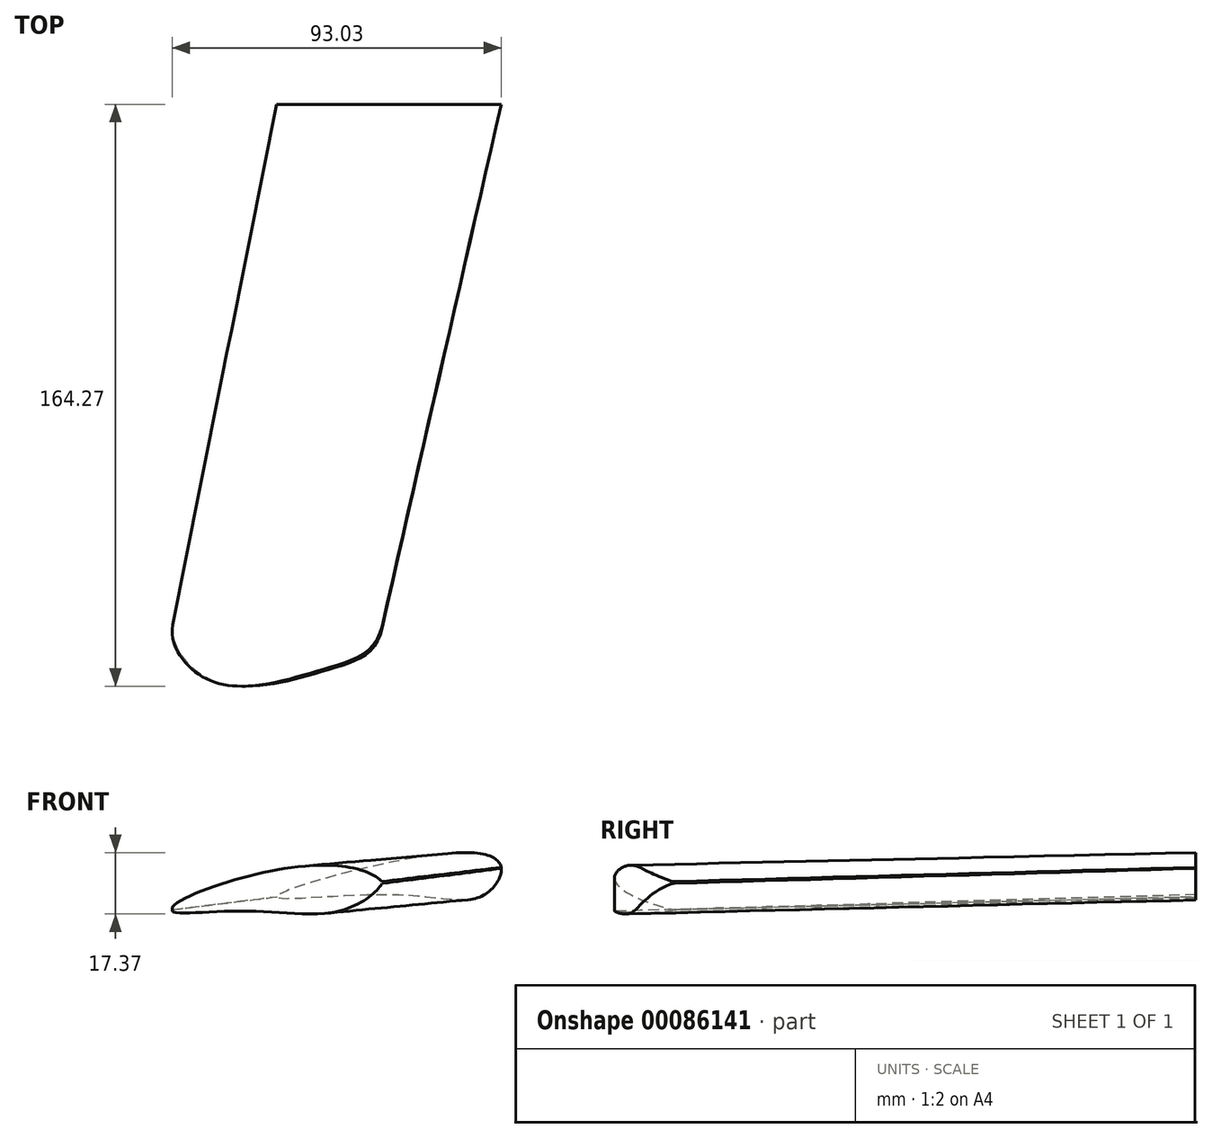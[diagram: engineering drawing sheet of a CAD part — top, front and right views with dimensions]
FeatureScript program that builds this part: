
annotation { "Feature Type Name" : "Feature", "Feature Type Description" : "" }
export const myFeature = defineFeature(function(context is Context, id is Id, definition is map)
    precondition{}
    {
        {
            var Q0;
            Q0=qCreatedBy(makeId("Front.planeOp"),FACE);
            var sketch = newSketch(context, id + "F0", { "sketchPlane" : qUnion([Q0])});
            skPoint(sketch, "E0.4.internal.orphan", {"position": v(0, 8.33) * mm});
            skFitSpline(sketch, "E1", {"points": [v(8.73, 20.08) * mm, v(-3.65, 24.53) * mm, v(-54.77, 12.14) * mm, v(-21.27, 12.62) * mm, v(3.33, 12.3) * mm, v(8.73, 20.08) * mm]});
            skLineSegment(sketch, "E2", {"start": v(8.73, 20.08) * mm, "end": v(-54.77, 12.14) * mm, "construction": true});
            skSolve(sketch);
        }
        {
            var Q0;
            Q0=qCreatedBy(makeId("Front.planeOp"),FACE);
            cPlane(context, id + "F1", {"entities" : qUnion([Q0]), "cplaneType" : CPlaneType.OFFSET, "offset" : 165.1 * mm, "width" : 152.4 * mm, "height" : 152.4 * mm});
        }
        {
            var Q0;
            Q0=sQuery(id+"F0.wireOp",EDGE,"E2");
            cPlane(context, id + "F2", {"entities" : qUnion([Q0]), "cplaneType" : CPlaneType.LINE_ANGLE, "offset" : 152.4 * mm, "angle" : 90 * degree, "width" : 152.4 * mm, "height" : 152.4 * mm});
        }
        {
            var Q0;
            Q0=qCreatedBy(id+"F2.planeOp",FACE);
            var sketch = newSketch(context, id + "F3", { "sketchPlane" : qUnion([Q0])});
            skPoint(sketch, "E3.0", {"position": v(11.15, 0) * mm});
            skPoint(sketch, "E4.0", {"position": v(-52.84, 0) * mm});
            skLineSegment(sketch, "E5", {"start": v(11.15, 0) * mm, "end": v(-26.76, -165.1) * mm});
            skLineSegment(sketch, "E6", {"start": v(-26.76, -165.1) * mm, "end": v(-86.03, -165.1) * mm});
            skLineSegment(sketch, "E7", {"start": v(-86.03, -165.1) * mm, "end": v(-52.84, 0) * mm});
            skLineSegment(sketch, "E8", {"start": v(-52.84, 0) * mm, "end": v(11.15, 0) * mm});
            skFitSpline(sketch, "E9", {"points": [v(-22.7, -147.39) * mm, v(-38.03, -159.35) * mm, v(-70.3, -163) * mm, v(-82.38, -146.93) * mm], "startDerivative": vector(-18.6, -81.04) * mm, "endDerivative": vector(11.87, 59.07) * mm});
            skSolve(sketch);
        }
        {
            var Q0;
            Q0=qCreatedBy(id+"F1.planeOp",FACE);
            var sketch = newSketch(context, id + "F4", { "sketchPlane" : qUnion([Q0])});
            skPoint(sketch, "E10.0", {"position": v(-87.7, 8.03) * mm});
            skPoint(sketch, "E11.0", {"position": v(-28.89, 15.38) * mm});
            skFitSpline(sketch, "E12", {"points": [v(-28.89, 15.38) * mm, v(-46.86, 20.76) * mm, v(-87.7, 8.03) * mm, v(-65.18, 8.03) * mm, v(-38.26, 8.03) * mm, v(-28.89, 15.38) * mm]});
            skSolve(sketch);
        }
        {
            var Q0;
            {var subQ0=sQuery(id+"F3.wireOp",EDGE,"E8");Q0=makeQuery(id+"F3.imprint","IMPRINT",FACE,{"disambiguationData":[TD([[makeQuery(id+"F3.imprint","IMPRINT",EDGE,{"derivedFrom":subQ0}),-1.0]])]});}
            extrude(context, id + "F5", {"entities" : qUnion([Q0]), "endBound" : BoundingType.SYMMETRIC, "depth" : 25.4 * mm});
        }
        {
            var Q1;
            Q1=qSketchRegion(id+"F0",true);
            var Q2;
            Q2=qSketchRegion(id+"F4",true);
            loft(context, id + "F6", {"sheetProfilesArray" : [{ "sheetProfileEntities" : qUnion([Q1]) }, { "sheetProfileEntities" : qUnion([Q2]) }]});
        }
        {
            var Q0;
            Q0=makeQuery(id+"F5.opExtrude","SWEPT_BODY",BODY,{"disambiguationData":[OSD([sQuery(id+"F3.wireOp",EDGE,"E5"),sQuery(id+"F3.wireOp",EDGE,"E7"),sQuery(id+"F3.wireOp",EDGE,"E8"),sQuery(id+"F3.wireOp",EDGE,"E9")])]});
            var Q1;
            Q1=makeQuery(id+"F6.opLoft","SWEPT_BODY",BODY,{"disambiguationData":[OSD([makeQuery(id+"F0.imprint","IMPRINT",FACE,{"disambiguationData":[TD([[makeQuery(id+"F0.imprint","IMPRINT",EDGE,{"derivedFrom":sQuery(id+"F0.wireOp",EDGE,"E1")}),1.0]])]}),makeQuery(id+"F4.imprint","IMPRINT",FACE,{"disambiguationData":[TD([[makeQuery(id+"F4.imprint","IMPRINT",EDGE,{"derivedFrom":sQuery(id+"F4.wireOp",EDGE,"E12")}),1.0]])]})])]});
            booleanBodies(context, id + "F7", {"operationType" : BooleanOperationType.INTERSECTION, "tools" : qUnion([Q0, Q1])});
        }
    });
